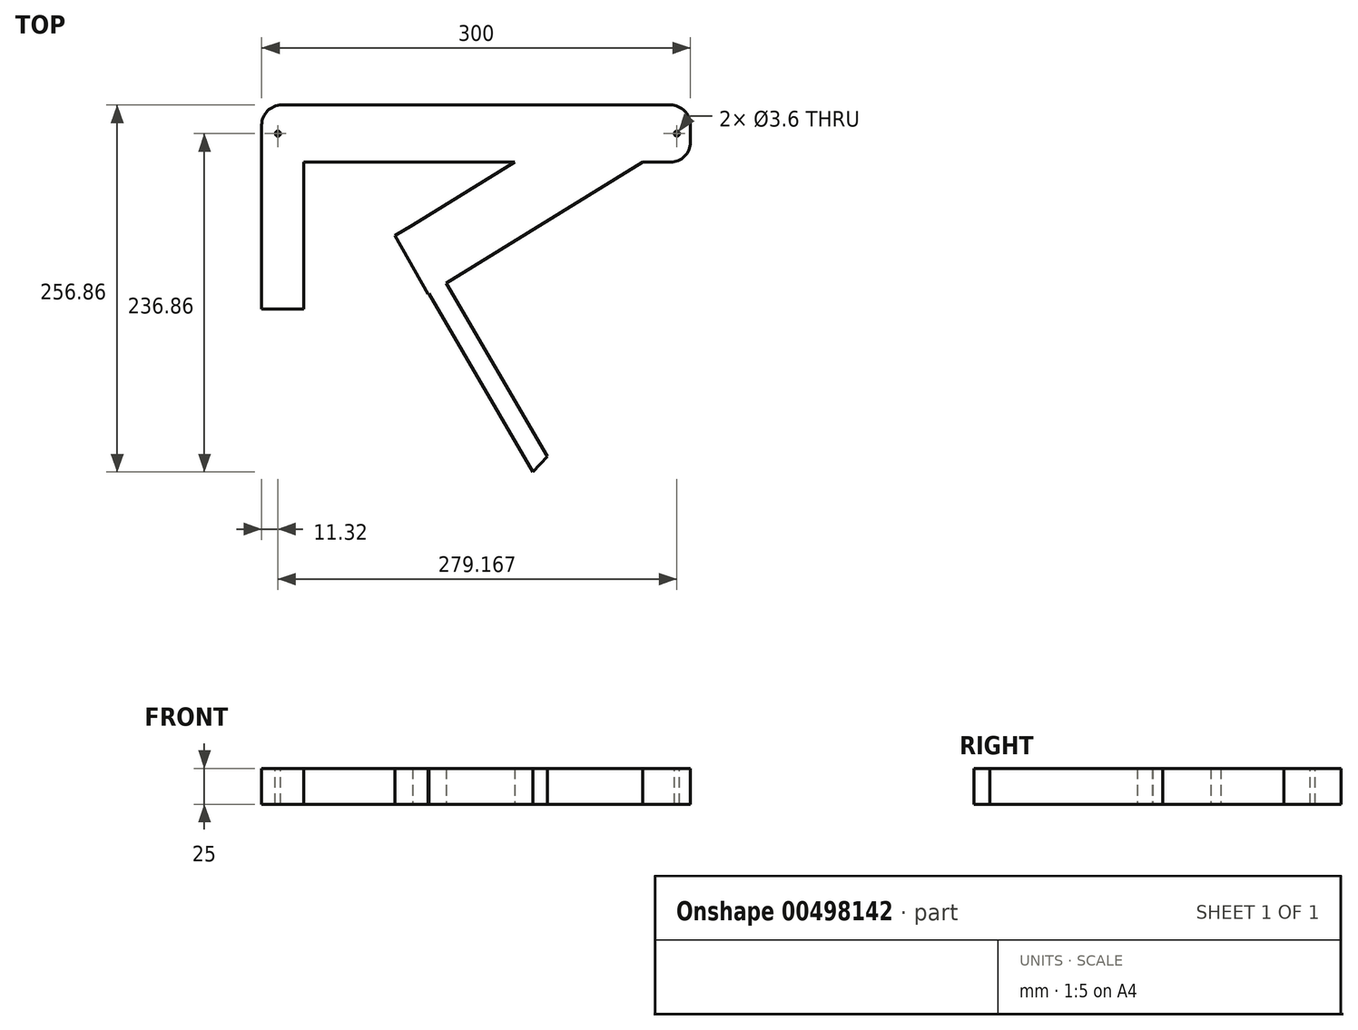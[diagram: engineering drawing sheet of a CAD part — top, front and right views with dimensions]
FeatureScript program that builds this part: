
annotation { "Feature Type Name" : "Feature", "Feature Type Description" : "" }
export const myFeature = defineFeature(function(context is Context, id is Id, definition is map)
    precondition{}
    {
        {
            var Q0;
            Q0=qCreatedBy(makeId("Top.planeOp"),FACE);
            var sketch = newSketch(context, id + "F0", { "sketchPlane" : qUnion([Q0])});
            skLineSegment(sketch, "E0.bottom", {"start": v(136, 20) * mm, "end": v(-136, 20) * mm});
            skLineSegment(sketch, "E0.top", {"start": v(136, -20) * mm, "end": v(-120.56, -20) * mm});
            skLineSegment(sketch, "E0.left", {"start": v(150, 6) * mm, "end": v(150, -6) * mm});
            skLineSegment(sketch, "E0.right", {"start": v(-150, 6) * mm, "end": v(-150, -6) * mm});
            skPoint(sketch, "E0.middle", {"position": v(0, 0) * mm});
            skPoint(sketch, "E1.visualSharp", {"position": v(-150, 20) * mm});
            skArc(sketch, "E1.filletArc", {"start": v(-136, 20) * mm, "mid": v(-145.9, 15.9) * mm, "end": v(-150, 6) * mm});
            skPoint(sketch, "E2.visualSharp", {"position": v(-150, -20) * mm});
            skPoint(sketch, "E3.visualSharp", {"position": v(150, 20) * mm});
            skArc(sketch, "E3.filletArc", {"start": v(150, 6) * mm, "mid": v(145.9, 15.9) * mm, "end": v(136, 20) * mm});
            skPoint(sketch, "E4.visualSharp", {"position": v(150, -20) * mm});
            skArc(sketch, "E4.filletArc", {"start": v(136, -20) * mm, "mid": v(145.9, -15.9) * mm, "end": v(150, -6) * mm});
            skLineSegment(sketch, "E5.bottom", {"start": v(-136, 20) * mm, "end": v(-120.56, 20) * mm});
            skLineSegment(sketch, "E5.top", {"start": v(-150, -122.79) * mm, "end": v(-120.56, -122.79) * mm});
            skLineSegment(sketch, "E5.left", {"start": v(-150, 6) * mm, "end": v(-150, -122.79) * mm});
            skLineSegment(sketch, "E5.right", {"start": v(-120.56, -20) * mm, "end": v(-120.56, -122.79) * mm});
            skLineSegment(sketch, "E6", {"start": v(91.79, 20) * mm, "end": v(-44.45, -64.1) * mm});
            skLineSegment(sketch, "E7", {"start": v(91.79, 20) * mm, "end": v(116.48, -20) * mm});
            skLineSegment(sketch, "E8", {"start": v(116.48, -20) * mm, "end": v(-20.78, -104.73) * mm});
            skLineSegment(sketch, "E9", {"start": v(-44.45, -64.1) * mm, "end": v(-20.78, -104.73) * mm});
            skLineSegment(sketch, "E10", {"start": v(-44.45, -64.1) * mm, "end": v(-56.77, -71.28) * mm});
            skLineSegment(sketch, "E11", {"start": v(-20.78, -104.73) * mm, "end": v(-33.72, -112.27) * mm});
            skLineSegment(sketch, "E12", {"start": v(-56.77, -71.28) * mm, "end": v(-33.72, -112.27) * mm});
            skLineSegment(sketch, "E13", {"start": v(-56.77, -71.28) * mm, "end": v(39.73, -236.86) * mm});
            skLineSegment(sketch, "E14", {"start": v(-44.45, -64.1) * mm, "end": v(49.86, -225.95) * mm});
            skLineSegment(sketch, "E15", {"start": v(49.86, -225.95) * mm, "end": v(39.73, -236.86) * mm});
            skSolve(sketch);
        }
        {
            var Q0;
            Q0 = qSketchRegion(id + "F0", true);
            extrude(context, id + "F1", {"entities" : qUnion([Q0]), "endBound" : BoundingType.SYMMETRIC, "depth" : 25 * mm, "offsetDistance" : 25 * mm});
        }
        {
            var Q0;
            Q0=makeQuery(id+"F1.opExtrude","CAP_FACE",FACE,{"disambiguationData":[OSD([sQuery(id+"F0.wireOp",EDGE,"E0.bottom"),sQuery(id+"F0.wireOp",EDGE,"E0.top"),sQuery(id+"F0.wireOp",EDGE,"E0.left"),sQuery(id+"F0.wireOp",EDGE,"E0.right")])],"isStart":false});
            var sketch = newSketch(context, id + "F2", { "sketchPlane" : qUnion([Q0])});
            skCircle(sketch, "E16", {"center": v(-138.68, 0) * mm, "radius": 1.8 * mm});
            skPoint(sketch, "E16.centerSnap0", {"position": v(-150, 0) * mm});
            skSolve(sketch);
        }
        {
            var Q0;
            Q0 = qSketchRegion(id + "F2", true);
            extrude(context, id + "F3", {"entities" : qUnion([Q0]), "operationType" : NewBodyOperationType.REMOVE, "oppositeDirection" : true, "depth" : 26 * mm, "offsetDistance" : 25 * mm});
        }
        {
            var Q0;
            Q0=makeQuery(id+"F1.opExtrude","CAP_FACE",FACE,{"disambiguationData":[OSD([sQuery(id+"F0.wireOp",EDGE,"E0.bottom"),sQuery(id+"F0.wireOp",EDGE,"E0.top"),sQuery(id+"F0.wireOp",EDGE,"E0.left"),sQuery(id+"F0.wireOp",EDGE,"E0.right")])],"isStart":false});
            var sketch = newSketch(context, id + "F4", { "sketchPlane" : qUnion([Q0])});
            skCircle(sketch, "E17", {"center": v(140.49, 0) * mm, "radius": 1.8 * mm});
            skPoint(sketch, "E17.centerSnap0", {"position": v(150, 0) * mm});
            skSolve(sketch);
        }
        {
            var Q0;
            Q0 = qSketchRegion(id + "F4", true);
            extrude(context, id + "F5", {"entities" : qUnion([Q0]), "operationType" : NewBodyOperationType.REMOVE, "oppositeDirection" : true, "depth" : 26 * mm, "offsetDistance" : 25 * mm});
        }
    });
